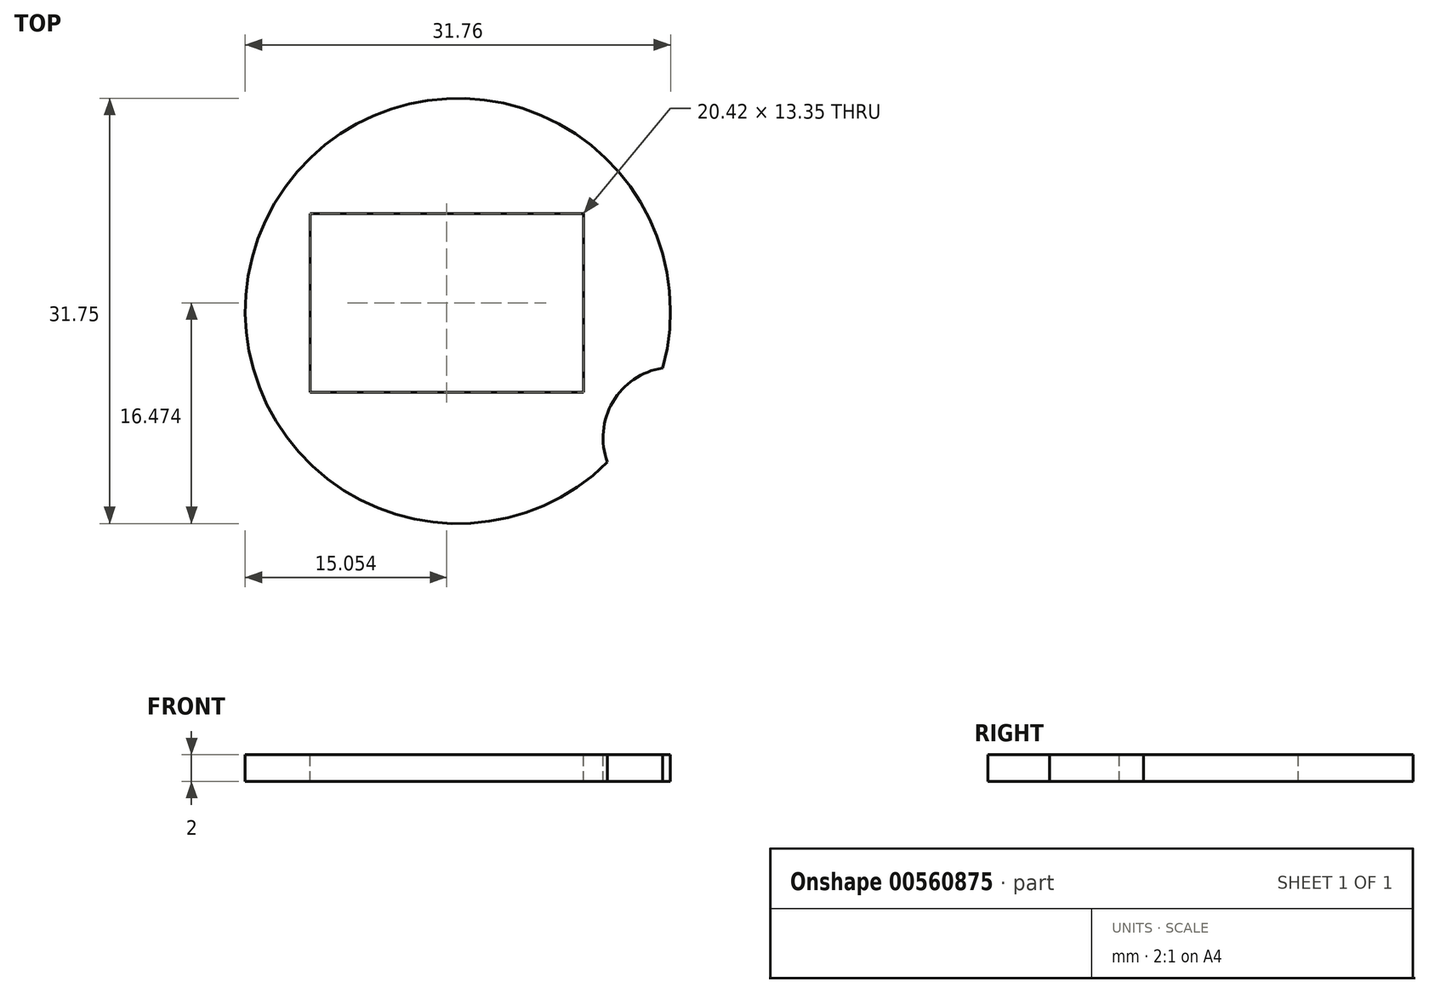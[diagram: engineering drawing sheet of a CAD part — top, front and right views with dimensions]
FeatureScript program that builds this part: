
annotation { "Feature Type Name" : "Feature", "Feature Type Description" : "" }
export const myFeature = defineFeature(function(context is Context, id is Id, definition is map)
    precondition{}
    {
        {
            var Q0;
            Q0=qCreatedBy(makeId("Top.planeOp"),FACE);
            var sketch = newSketch(context, id + "F0", { "sketchPlane" : qUnion([Q0])});
            skCircle(sketch, "E0", {"center": v(0, 0) * mm, "radius": 15.88 * mm});
            skSolve(sketch);
        }
        {
            var Q0;
            Q0=qSketchRegion(id+"F0",true);
            extrude(context, id + "F1", {"entities" : qUnion([Q0]), "depth" : 2 * mm, "offsetDistance" : 25 * mm});
        }
        {
            var Q0;
            Q0=makeQuery(id+"F1.opExtrude","CAP_FACE",FACE,{"disambiguationData":[OSD([sQuery(id+"F0.wireOp",EDGE,"E0")])],"isStart":false});
            var sketch = newSketch(context, id + "F2", { "sketchPlane" : qUnion([Q0])});
            skLineSegment(sketch, "E1.bottom", {"start": v(-11.04, 7.28) * mm, "end": v(9.38, 7.28) * mm});
            skLineSegment(sketch, "E1.top", {"start": v(-11.04, -6.07) * mm, "end": v(9.38, -6.07) * mm});
            skLineSegment(sketch, "E1.left", {"start": v(-11.04, 7.28) * mm, "end": v(-11.04, -6.07) * mm});
            skLineSegment(sketch, "E1.right", {"start": v(9.38, 7.28) * mm, "end": v(9.38, -6.07) * mm});
            skSolve(sketch);
        }
        {
            var Q0;
            Q0=qSketchRegion(id+"F2",true);
            extrude(context, id + "F3", {"entities" : qUnion([Q0]), "operationType" : NewBodyOperationType.REMOVE, "oppositeDirection" : true, "depth" : 2 * mm, "offsetDistance" : 25 * mm});
        }
        {
            var Q0;
            Q0=makeQuery(id+"F1.opExtrude","CAP_FACE",FACE,{"disambiguationData":[OSD([sQuery(id+"F0.wireOp",EDGE,"E0")])],"isStart":false});
            var sketch = newSketch(context, id + "F4", { "sketchPlane" : qUnion([Q0])});
            skCircle(sketch, "E2", {"center": v(16.1, -9.46) * mm, "radius": 5.27 * mm});
            skSolve(sketch);
        }
        {
            var Q0;
            Q0 = qSketchRegion(id + "F4", true);
            extrude(context, id + "F5", {"entities" : qUnion([Q0]), "operationType" : NewBodyOperationType.REMOVE, "oppositeDirection" : true, "depth" : 5 * mm, "offsetDistance" : 25 * mm});
        }
    });
